# Revit family: steigeleiter_8_FT_FTSO_FTK_A2_A4.800rfa
name_source: partatom
category: Generic Models
revit_build: Autodesk Revit 2017 (Build: 20160225_1515(x64)
units: mm (PartAtom-declared; Revit-internal decimal feet)

## family parameters
Always vertical = Yes
Can host rebar = No
Cut with Voids When Loaded = No
Part Type = Normal
Room Calculation Point = No
Round Connector Dimension = Use Diameter
Shared = No
Work Plane-Based = No

## types (1)
- SLM 50 C40 8 FT
    Article Type = SLM 50 C40 8 FT
    Cut's number = 60
    Cut's number 2 = 5
    Cut's number 3 = 2
    Cut's space = 50 mm  [stored 0.164042 ft]
    Cut's space 2 = 600 mm
    GTIN = 4012196168736
    Length = 3000 mm  [stored 9.84252 ft]
    Length 2 = 274 mm
    Manufacturer = OBO BETTERMANN
    Manufacturer Art.No. = 6010520
    Material = Hot-dip galvanised
    URL = http://www.obo-bettermann.com
    Width = 800 mm  [stored 2.62467 ft]
    Width 1 = 400 mm  [stored 1.31234 ft]

note: [stored X ft] marks values corroborated as IEEE doubles in the binary element streams (Revit-internal decimal feet)

## geometry (parser evidence)
native form markers: Sweep x1
no freeform markers — native parametric forms only
